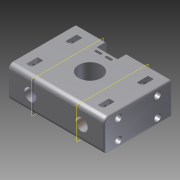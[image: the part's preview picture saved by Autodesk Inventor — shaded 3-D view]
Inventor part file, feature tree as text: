
AUTODESK INVENTOR PART (.ipt)
format: ipt  version: 2012 (Build 160160000, 160)  size: 321,024 bytes
history: native  units: mm
features: extrude x13, sketch x13, fillet x2, plane x2
ambient origin geometry x8: Origin, YZ Plane, XZ Plane, XY Plane, X Axis, Y Axis, Z Axis, Center Point
bodies: Solid1 (feature_tree)
feature tree (30):
  extrude  "Extrusion1"  Depth=60.0mm
  extrude  "Extrusion2"  Depth=30.0mm
  fillet  "Fillet1"  Radius=10.0mm
  fillet  "Fillet2"  Radius=20.0mm
  extrude  "Extrusion3"  Depth=4.0mm
  plane  "Work Plane2"
  plane  "Work Plane3"
  extrude  "Extrusion9"  Depth=9.0mm
  extrude  "Extrusion11"  Depth=4.0mm
  extrude  "Extrusion12"  Depth=9.0mm
  extrude  "Extrusion13"  TaperAngle=0.0deg  [1 undecoded]
  extrude  "Extrusion14"  Depth=3.0mm
  extrude  "Extrusion15"  Depth=7.1mm
  extrude  "Extrusion16"  Depth=6.0mm
  extrude  "Extrusion5"  Depth=5.45mm
  extrude  "Extrusion6"  Depth=16.0mm
  extrude  "Extrusion8"  Depth=22.0mm
  sketch  "Sketch1"  dims[d0=42.4mm d1=60.0mm]
  sketch  "Sketch2"  dims[d2=21.2mm d3=30.0mm d4=10.0mm d5=20.0mm d6=0.0mm]
  sketch  "Sketch3"  dims[d7=4.2mm d8=4.0mm]
  sketch  "Sketch5"  dims[d9=9.0mm d10=9.0mm]
  sketch  "Sketch6"  dims[d11=4.0mm d12=4.0mm]
  sketch  "Sketch7"  dims[d13=4.0mm d14=9.0mm]
  sketch  "Sketch8"  dims[d15=9.0mm d16=0.0mm d17=0.0mm]
  sketch  "Sketch11"  dims[d18=1.0mm d19=3.0mm]
  sketch  "Sketch12"  dims[d20=3.5mm d21=7.1mm]
  sketch  "Sketch14"  dims[d22=6.0mm d23=6.0mm]
  sketch  "Sketch15"  dims[d24=5.45mm d25=5.45mm]
  sketch  "Sketch16"  dims[d26=20.0mm d27=0.0mm d31=16.0mm]
  sketch  "Sketch17"  dims[d32=3.1mm d33=22.0mm d34=3.0mm d35=0.0mm d36=5.6mm d37=8.0mm d38=0.0mm d39=23.5mm d40=30.5mm d41=15.25mm d42=11.75mm d45=2.5mm d46=0.0mm d47=-16.0mm d48=-16.0mm d49=12.0mm d50=0.0mm d51=7.0mm d61=10.0mm d62=10.0mm d63=4.1mm d64=14.0mm d65=14.0mm d66=5.0mm d67=0.0mm d68=7.5mm d69=6.0mm d70=0.0mm d71=13.0mm d72=10.0mm d74=6.0mm d75=0.0mm d76=2.1mm d77=5.0mm d78=5.0mm d79=6.5mm d80=3.25mm d81=14.0mm d82=0.0mm d83=4.1mm d84=6.5mm d85=1.2mm d86=1.5mm d87=1.5mm d88=8.0mm d89=0.0mm d90=19.0mm d91=14.2mm d92=15.5mm d93=0.0mm]
note: 1 required parameter value undecoded (feature->parameter linkage not recoverable at this tier; creation-order binding heuristic only, values carry confidence <= 0.55)
